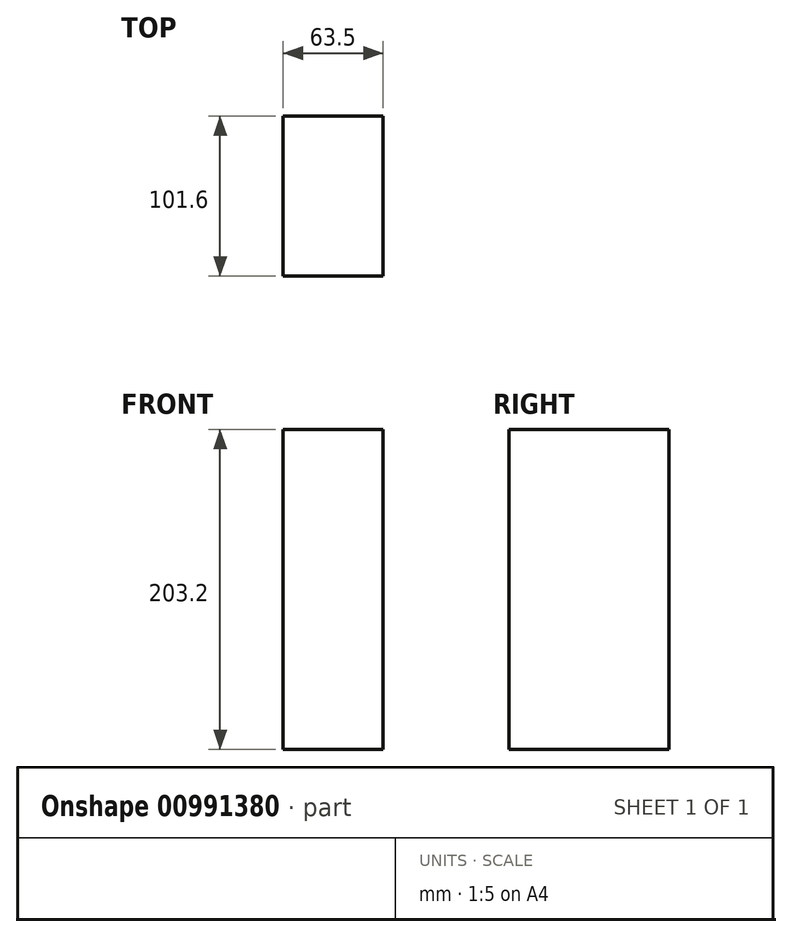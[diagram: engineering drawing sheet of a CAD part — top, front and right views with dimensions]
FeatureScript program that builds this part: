
annotation { "Feature Type Name" : "Feature", "Feature Type Description" : "" }
export const myFeature = defineFeature(function(context is Context, id is Id, definition is map)
    precondition{}
    {
        {
            var Q0;
            Q0=qCreatedBy(makeId("Top.planeOp"),FACE);
            var sketch = newSketch(context, id + "F0", { "sketchPlane" : qUnion([Q0])});
            skLineSegment(sketch, "E0.bottom", {"start": v(31.75, 50.8) * mm, "end": v(-31.75, 50.8) * mm});
            skLineSegment(sketch, "E0.top", {"start": v(31.75, -50.8) * mm, "end": v(-31.75, -50.8) * mm});
            skLineSegment(sketch, "E0.left", {"start": v(31.75, 50.8) * mm, "end": v(31.75, -50.8) * mm});
            skLineSegment(sketch, "E0.right", {"start": v(-31.75, 50.8) * mm, "end": v(-31.75, -50.8) * mm});
            skPoint(sketch, "E0.middle", {"position": v(0, 0) * mm});
            skSolve(sketch);
        }
        {
            var Q0;
            Q0 = qSketchRegion(id + "F0", true);
            extrude(context, id + "F1", {"entities" : qUnion([Q0]), "endBound" : BoundingType.SYMMETRIC, "depth" : 203.2 * mm, "offsetDistance" : 25.4 * mm});
        }
    });
